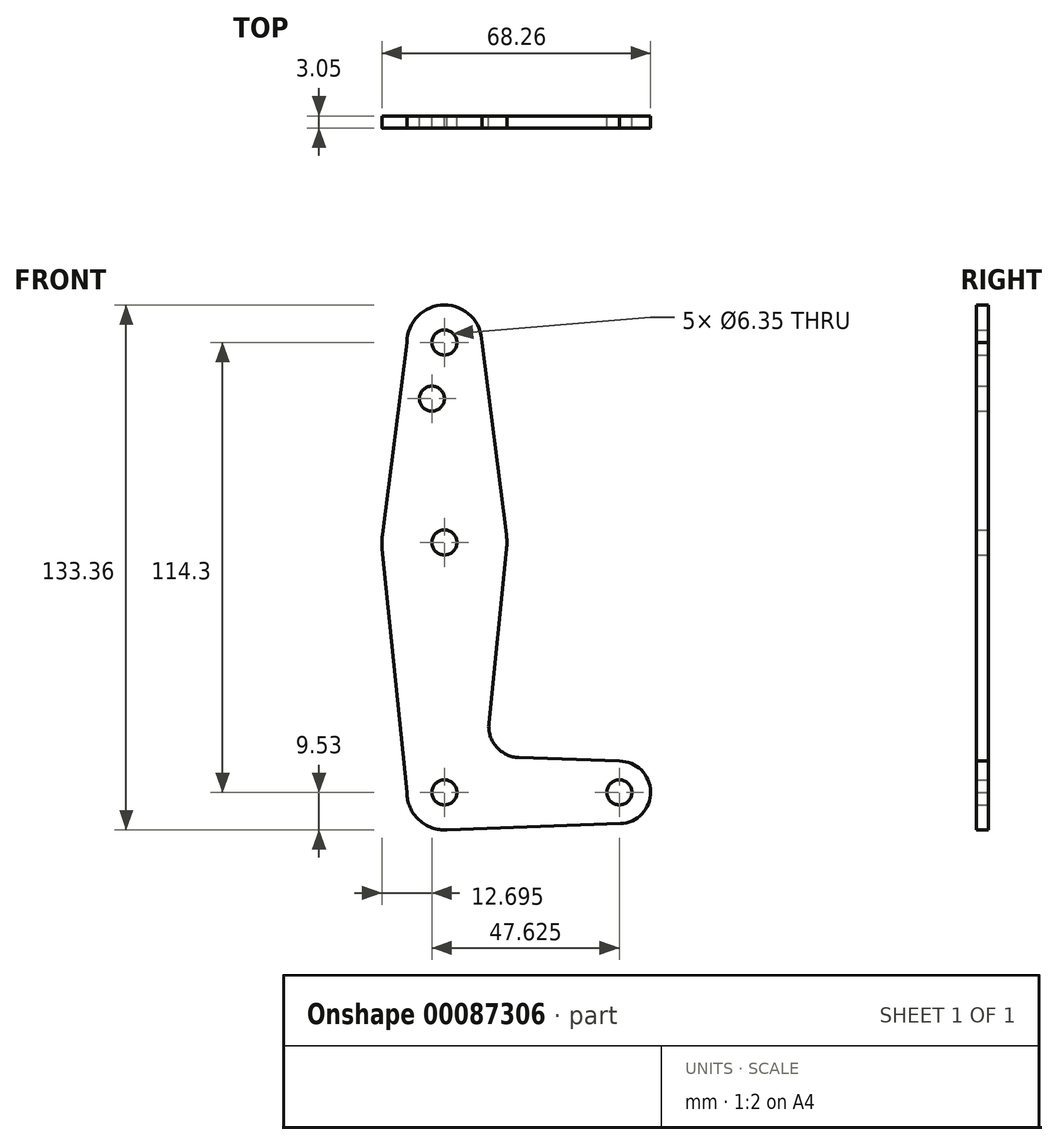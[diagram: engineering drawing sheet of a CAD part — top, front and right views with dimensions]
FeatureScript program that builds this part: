
annotation { "Feature Type Name" : "Feature", "Feature Type Description" : "" }
export const myFeature = defineFeature(function(context is Context, id is Id, definition is map)
    precondition{}
    {
        {
            var Q0;
            Q0=qCreatedBy(makeId("Front.planeOp"),FACE);
            var sketch = newSketch(context, id + "F0", { "sketchPlane" : qUnion([Q0])});
            skLineSegment(sketch, "E0", {"start": v(0, 0) * mm, "end": v(44.45, 0) * mm, "construction": true});
            skLineSegment(sketch, "E1", {"start": v(0, 0) * mm, "end": v(0, 63.5) * mm, "construction": true});
            skLineSegment(sketch, "E2", {"start": v(0, 63.5) * mm, "end": v(0, 114.3) * mm, "construction": true});
            skCircle(sketch, "E3", {"center": v(0, 63.5) * mm, "radius": 15.88 * mm});
            skCircle(sketch, "E4", {"center": v(0, 114.3) * mm, "radius": 9.53 * mm});
            skCircle(sketch, "E5", {"center": v(0, 0) * mm, "radius": 9.53 * mm});
            skCircle(sketch, "E6", {"center": v(44.45, 0) * mm, "radius": 7.94 * mm});
            skLineSegment(sketch, "E7", {"start": v(18.93, 8.85) * mm, "end": v(44.45, 7.94) * mm});
            skLineSegment(sketch, "E8", {"start": v(0, -9.53) * mm, "end": v(44.73, -7.93) * mm});
            skLineSegment(sketch, "E9", {"start": v(9.53, 114.3) * mm, "end": v(15.75, 65.5) * mm});
            skLineSegment(sketch, "E10", {"start": v(-9.53, 114.3) * mm, "end": v(-15.75, 65.5) * mm});
            skLineSegment(sketch, "E11", {"start": v(-9.53, 0) * mm, "end": v(-15.8, 61.9) * mm});
            skLineSegment(sketch, "E12", {"start": v(11.3, 17.6) * mm, "end": v(15.8, 61.9) * mm});
            skCircle(sketch, "E13", {"center": v(0, 114.3) * mm, "radius": 3.18 * mm});
            skCircle(sketch, "E14", {"center": v(0, 63.5) * mm, "radius": 3.18 * mm});
            skCircle(sketch, "E15", {"center": v(0, 0) * mm, "radius": 3.18 * mm});
            skCircle(sketch, "E16", {"center": v(44.45, 0) * mm, "radius": 3.18 * mm});
            skArc(sketch, "E17.filletArc", {"start": v(11.3, 17.6) * mm, "mid": v(13.22, 11.57) * mm, "end": v(18.93, 8.85) * mm});
            skCircle(sketch, "E18", {"center": v(-3.18, 100.03) * mm, "radius": 3.18 * mm});
            skSolve(sketch);
        }
        {
            var Q0;
            Q0 = qSketchRegion(id + "F0", true);
            extrude(context, id + "F1", {"entities" : qUnion([Q0]), "depth" : 3.05 * mm});
        }
    });
